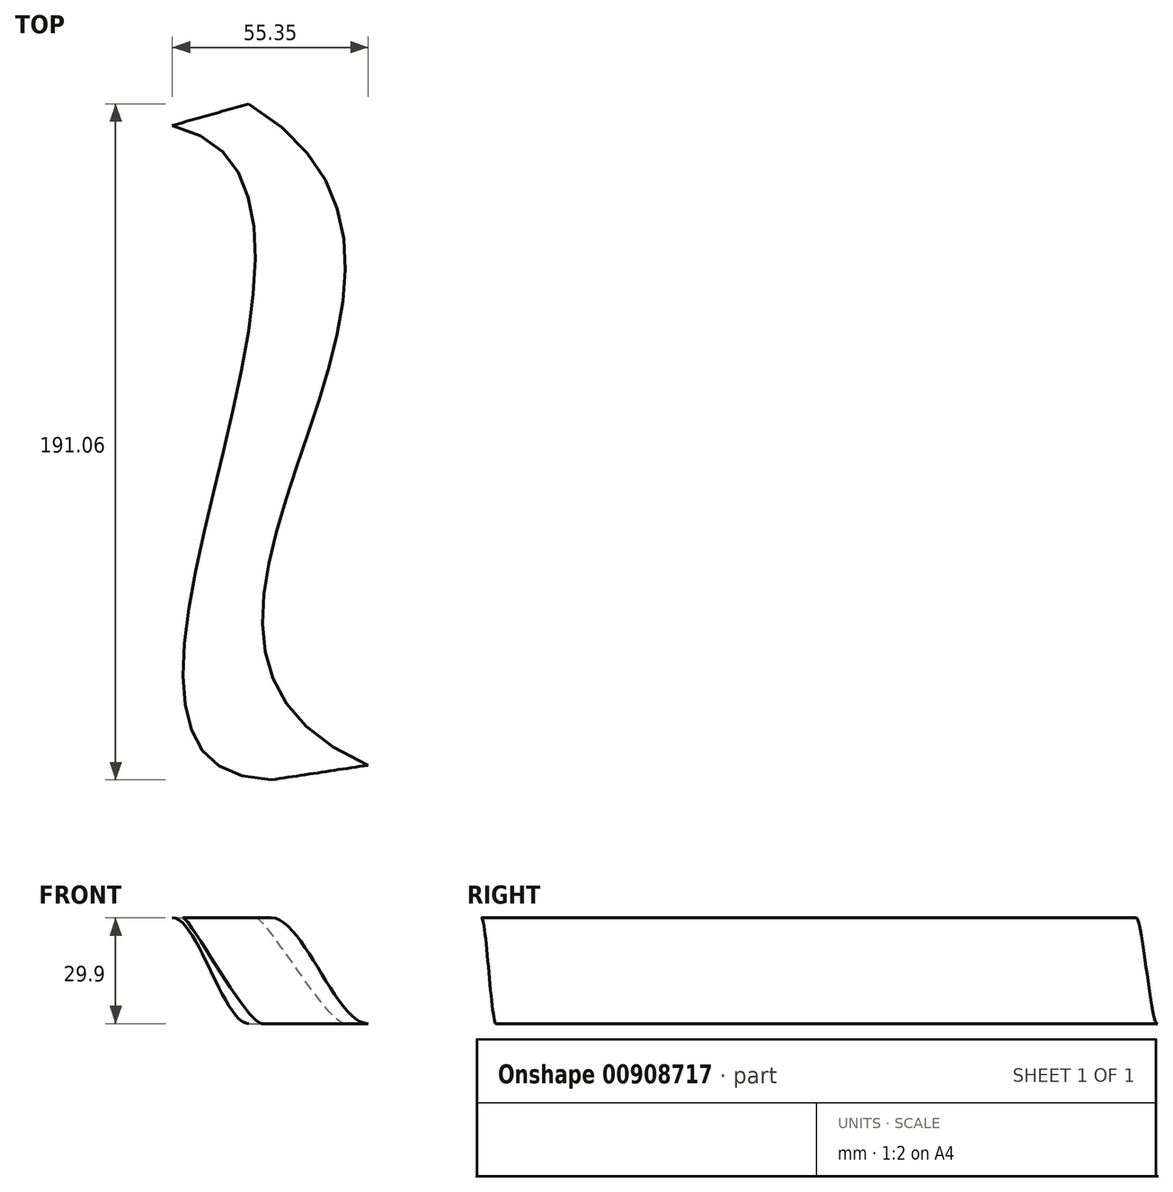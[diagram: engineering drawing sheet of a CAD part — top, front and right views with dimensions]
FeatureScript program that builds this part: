
annotation { "Feature Type Name" : "Feature", "Feature Type Description" : "" }
export const myFeature = defineFeature(function(context is Context, id is Id, definition is map)
    precondition{}
    {
        {
            var Q0;
            Q0=qCreatedBy(makeId("Top.planeOp"),FACE);
            var sketch = newSketch(context, id + "F0", { "sketchPlane" : qUnion([Q0])});
            skFitSpline(sketch, "E0", {"points": [v(39.66, 66.84) * mm, v(73.4, -120.1) * mm], "startDerivative": vector(241.47, -146.83) * mm, "endDerivative": vector(255.3, -111.37) * mm});
            skSolve(sketch);
        }
        {
            var Q0;
            Q0=qCreatedBy(makeId("Top.planeOp"),FACE);
            cPlane(context, id + "F1", {"entities" : qUnion([Q0]), "cplaneType" : CPlaneType.OFFSET, "offset" : 29.9 * mm, "width" : 150 * mm, "height" : 150 * mm});
        }
        {
            var Q0;
            Q0=qCreatedBy(id+"F1.planeOp",FACE);
            var sketch = newSketch(context, id + "F2", { "sketchPlane" : qUnion([Q0])});
            skFitSpline(sketch, "E1", {"points": [v(18.05, 60.72) * mm, v(45.97, -124.22) * mm], "startDerivative": vector(207.34, -47.06) * mm, "endDerivative": vector(214.92, -4.03) * mm});
            skSolve(sketch);
        }
        {
            var Q0;
            Q0=sQuery(id+"F2.wireOp",EDGE,"E1");
            var Q1;
            Q1=sQuery(id+"F0.wireOp",EDGE,"E0");
            loft(context, id + "F3", {"bodyType" : ToolBodyType.SURFACE, "startCondition" : LoftEndDerivativeType.TANGENT_TO_PROFILE, "startMagnitude" : 1, "endCondition" : LoftEndDerivativeType.TANGENT_TO_PROFILE, "endMagnitude" : 1, "wireProfilesArray" : [{ "wireProfileEntities" : qUnion([Q0]) }, { "wireProfileEntities" : qUnion([Q1]) }]});
        }
    });
